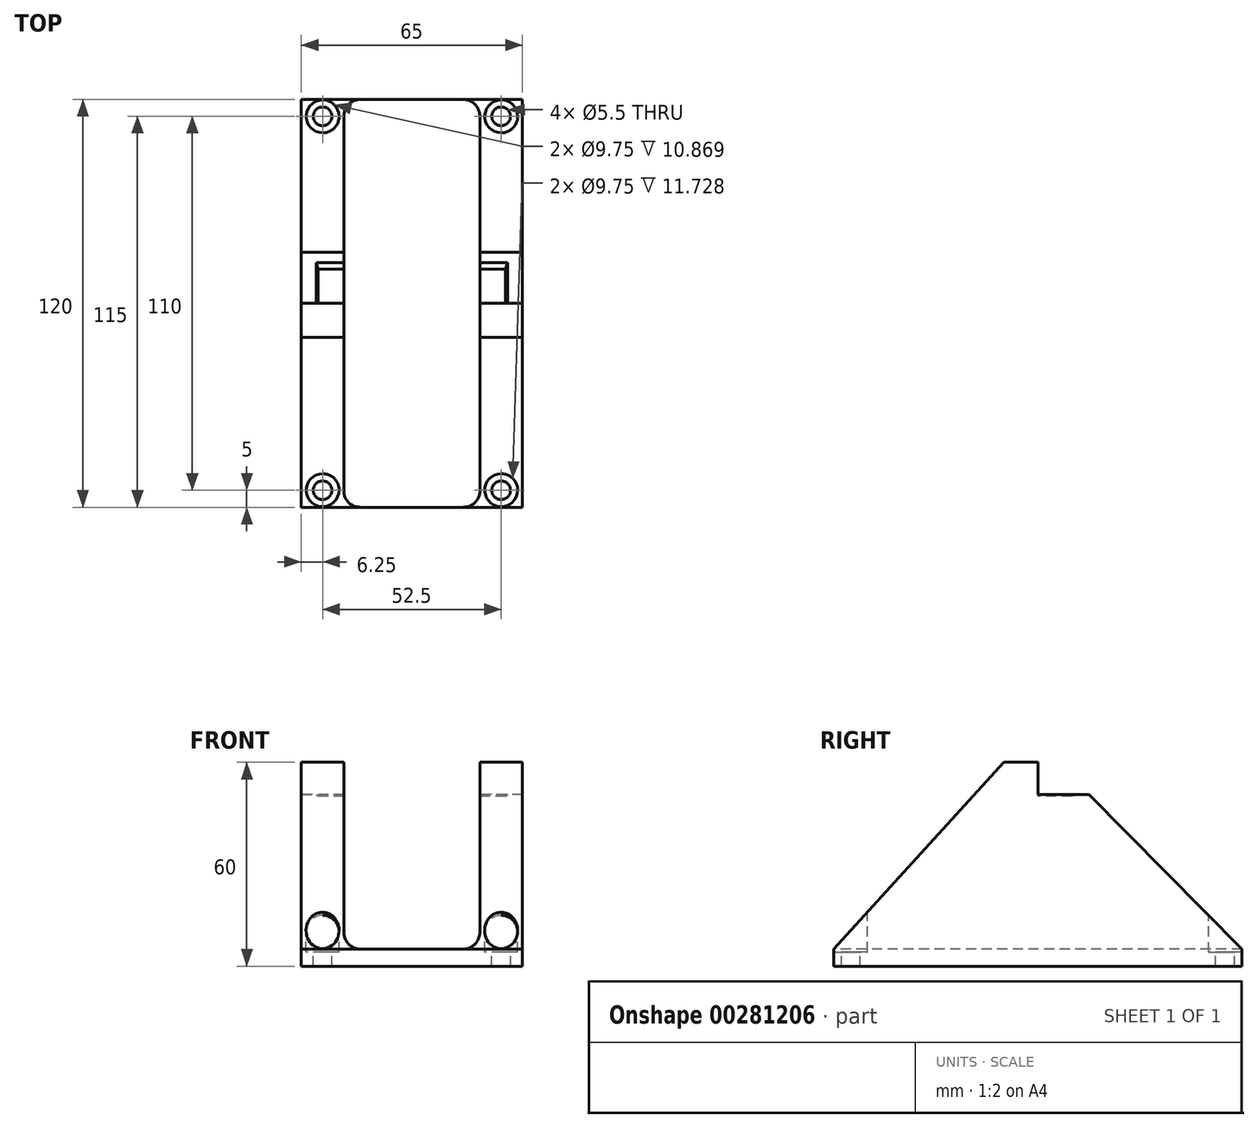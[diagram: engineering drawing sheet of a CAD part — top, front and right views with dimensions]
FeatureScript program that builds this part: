
annotation { "Feature Type Name" : "Feature", "Feature Type Description" : "" }
export const myFeature = defineFeature(function(context is Context, id is Id, definition is map)
    precondition{}
    {
        {
            var Q0;
            Q0=qCreatedBy(makeId("Right.planeOp"),FACE);
            var sketch = newSketch(context, id + "F0", { "sketchPlane" : qUnion([Q0])});
            skLineSegment(sketch, "E0", {"start": v(0, 60) * mm, "end": v(0, 50) * mm});
            skLineSegment(sketch, "E1", {"start": v(0, 50) * mm, "end": v(10, 50) * mm});
            skLineSegment(sketch, "E2", {"start": v(10, 50) * mm, "end": v(12, 50.54) * mm});
            skLineSegment(sketch, "E3", {"start": v(12, 50.54) * mm, "end": v(15, 50.54) * mm});
            skLineSegment(sketch, "E4", {"start": v(60, 0) * mm, "end": v(-60, 0) * mm});
            skLineSegment(sketch, "E5", {"start": v(-10, 60) * mm, "end": v(0, 60) * mm});
            skLineSegment(sketch, "E6", {"start": v(-60, 0) * mm, "end": v(-60, 5) * mm});
            skLineSegment(sketch, "E7", {"start": v(-60, 5) * mm, "end": v(-10, 60) * mm});
            skLineSegment(sketch, "E8", {"start": v(60, 0) * mm, "end": v(60, 5) * mm});
            skLineSegment(sketch, "E9", {"start": v(60, 5) * mm, "end": v(15, 50.54) * mm});
            skPoint(sketch, "E10", {"position": v(0, 0) * mm});
            skSolve(sketch);
        }
        {
            var Q0;
            Q0 = qSketchRegion(id + "F0", true);
            extrude(context, id + "F1", {"entities" : qUnion([Q0]), "endBound" : BoundingType.SYMMETRIC, "depth" : 65 * mm, "offsetDistance" : 25 * mm});
        }
        {
            var Q0;
            Q0=qCreatedBy(makeId("Front.planeOp"),FACE);
            var sketch = newSketch(context, id + "F2", { "sketchPlane" : qUnion([Q0])});
            skLineSegment(sketch, "E11.bottom", {"start": v(20, 5) * mm, "end": v(-20, 5) * mm});
            skLineSegment(sketch, "E11.top", {"start": v(20, 60) * mm, "end": v(-20, 60) * mm});
            skLineSegment(sketch, "E11.left", {"start": v(20, 5) * mm, "end": v(20, 60) * mm});
            skLineSegment(sketch, "E11.right", {"start": v(-20, 5) * mm, "end": v(-20, 60) * mm});
            skPoint(sketch, "E11.middle", {"position": v(0, 32.5) * mm});
            skSolve(sketch);
        }
        {
            var Q0;
            Q0 = qSketchRegion(id + "F2", true);
            extrude(context, id + "F3", {"entities" : qUnion([Q0]), "operationType" : NewBodyOperationType.REMOVE, "endBound" : BoundingType.THROUGH_ALL, "oppositeDirection" : true, "depth" : 25 * mm, "offsetDistance" : 25 * mm, "hasSecondDirection" : true, "secondDirectionBound" : SecondDirectionBoundingType.THROUGH_ALL, "secondDirectionOppositeDirection" : false, "secondDirectionDepth" : 25 * mm});
        }
        {
            var Q0;
            Q0=makeQuery(id+"F3.boolean.opBoolean","COPY",EDGE,{"derivedFrom":makeQuery(id+"F3.opExtrude","SWEPT_EDGE",EDGE,{"disambiguationData":[OSD([sQuery(id+"F2.wireOp",EDGE,"E11.bottom"),sQuery(id+"F2.wireOp",EDGE,"E11.left")])]})});
            var Q1;
            Q1=makeQuery(id+"F3.boolean.opBoolean","COPY",EDGE,{"derivedFrom":makeQuery(id+"F3.opExtrude","SWEPT_EDGE",EDGE,{"disambiguationData":[OSD([sQuery(id+"F2.wireOp",EDGE,"E11.bottom"),sQuery(id+"F2.wireOp",EDGE,"E11.right")])]})});
            fillet(context, id + "F4", {"entities" : qUnion([Q0, Q1]), "radius" : 5 * mm, "tangentPropagation" : true, "allowEdgeOverflow" : false});
        }
        {
            var Q0;
            {var subQ2=sQuery(id+"F0.wireOp",EDGE,"E1");Q0=makeQuery(id+"F3.boolean.opBoolean","SPLIT",FACE,{"disambiguationData":[TD([makeQuery(id+"F3.opExtrude","SWEPT_FACE",FACE,{"disambiguationData":[OSD([sQuery(id+"F2.wireOp",EDGE,"E11.right")])]})])],"derivedFrom":makeQuery(id+"F1.opExtrude","SWEPT_FACE",FACE,{"disambiguationData":[OSD([subQ2])]})});}
            var sketch = newSketch(context, id + "F5", { "sketchPlane" : qUnion([Q0])});
            skLineSegment(sketch, "E12.bottom", {"start": v(-26.25, 55) * mm, "end": v(26.25, 55) * mm, "construction": true});
            skLineSegment(sketch, "E12.top", {"start": v(-26.25, -55) * mm, "end": v(26.25, -55) * mm, "construction": true});
            skLineSegment(sketch, "E12.left", {"start": v(-26.25, 55) * mm, "end": v(-26.25, -55) * mm, "construction": true});
            skLineSegment(sketch, "E12.right", {"start": v(26.25, 55) * mm, "end": v(26.25, -55) * mm, "construction": true});
            skPoint(sketch, "E12.middle", {"position": v(0, 0) * mm});
            skPoint(sketch, "E13", {"position": v(-26.25, 55) * mm});
            skPoint(sketch, "E14", {"position": v(26.25, 55) * mm});
            skPoint(sketch, "E15", {"position": v(26.25, -55) * mm});
            skPoint(sketch, "E16", {"position": v(-26.25, -55) * mm});
            skSolve(sketch);
        }
        {
            var Q0;
            Q0=sQuery(id+"F5.wireOp",VERTEX,"E13");
            var Q1;
            Q1=sQuery(id+"F5.wireOp",VERTEX,"E14");
            var Q2;
            Q2=sQuery(id+"F5.wireOp",VERTEX,"E16");
            var Q3;
            Q3=sQuery(id+"F5.wireOp",VERTEX,"E15");
            var Q4;
            Q4=makeQuery(id+"F1.opExtrude","SWEPT_BODY",BODY,{"disambiguationData":[OSD([sQuery(id+"F0.wireOp",EDGE,"E0"),sQuery(id+"F0.wireOp",EDGE,"E1"),sQuery(id+"F0.wireOp",EDGE,"E2"),sQuery(id+"F0.wireOp",EDGE,"E3"),sQuery(id+"F0.wireOp",EDGE,"E4"),sQuery(id+"F0.wireOp",EDGE,"E5"),sQuery(id+"F0.wireOp",EDGE,"E6"),sQuery(id+"F0.wireOp",EDGE,"E7"),sQuery(id+"F0.wireOp",EDGE,"E8"),sQuery(id+"F0.wireOp",EDGE,"E9")])]});
            hole(context, id + "F6", {"style" : HoleStyle.C_BORE, "endStyle" : HoleEndStyle.THROUGH, "holeDiameter" : 5.5 * mm, "cBoreDiameter" : 9.75 * mm, "cBoreDepth" : 1 * mm, "majorDiameter" : 5 * mm, "isTappedThrough" : true, "tappedDepth" : 12 * mm, "tapClearance" : 3, "locations" : qUnion([Q0, Q1, Q2, Q3]), "scope" : qUnion([Q4])});
        }
        {
            var Q0;
            {var subQ2=sQuery(id+"F0.wireOp",EDGE,"E1");Q0=makeQuery(id+"F3.boolean.opBoolean","SPLIT",FACE,{"disambiguationData":[TD([makeQuery(id+"F3.opExtrude","SWEPT_FACE",FACE,{"disambiguationData":[OSD([sQuery(id+"F2.wireOp",EDGE,"E11.left")])]})])],"derivedFrom":makeQuery(id+"F1.opExtrude","SWEPT_FACE",FACE,{"disambiguationData":[OSD([subQ2])]})});}
            var sketch = newSketch(context, id + "F7", { "sketchPlane" : qUnion([Q0])});
            skLineSegment(sketch, "E17.bottom", {"start": v(-32.5, 0) * mm, "end": v(-27.5, 0) * mm});
            skLineSegment(sketch, "E17.top", {"start": v(-32.5, 12) * mm, "end": v(-27.5, 12) * mm});
            skLineSegment(sketch, "E17.left", {"start": v(-32.5, 0) * mm, "end": v(-32.5, 12) * mm});
            skLineSegment(sketch, "E17.right", {"start": v(-27.5, 0) * mm, "end": v(-27.5, 12) * mm});
            skLineSegment(sketch, "E18", {"start": v(0, 0) * mm, "end": v(0, 44.26) * mm, "construction": true});
            skLineSegment(sketch, "E19.MirrorCS", {"start": v(32.5, 0) * mm, "end": v(27.5, 0) * mm});
            skLineSegment(sketch, "E20.MirrorCS", {"start": v(32.5, 12) * mm, "end": v(27.5, 12) * mm});
            skLineSegment(sketch, "E21.MirrorCS", {"start": v(32.5, 0) * mm, "end": v(32.5, 12) * mm});
            skLineSegment(sketch, "E22.MirrorCS", {"start": v(27.5, 0) * mm, "end": v(27.5, 12) * mm});
            skSolve(sketch);
        }
        {
            var Q0;
            Q0 = qSketchRegion(id + "F7", true);
            var Q1;
            {var subQ1=sQuery(id+"F0.wireOp",EDGE,"E3");Q1=makeQuery(id+"F3.boolean.opBoolean","SPLIT",FACE,{"disambiguationData":[TD([makeQuery(id+"F3.opExtrude","SWEPT_FACE",FACE,{"disambiguationData":[OSD([sQuery(id+"F2.wireOp",EDGE,"E11.left")])]})])],"derivedFrom":makeQuery(id+"F1.opExtrude","SWEPT_FACE",FACE,{"disambiguationData":[OSD([subQ1])]})});}
            extrude(context, id + "F8", {"entities" : qUnion([Q0]), "operationType" : NewBodyOperationType.ADD, "endBound" : BoundingType.UP_TO_SURFACE, "depth" : 25 * mm, "endBoundEntityFace" : qUnion([Q1]), "offsetDistance" : 25 * mm});
        }
        {
            var Q0;
            Q0=makeQuery(id+"F8.opExtrude","CAP_EDGE",EDGE,{"disambiguationData":[OSD([sQuery(id+"F7.wireOp",EDGE,"E22.MirrorCS")])],"isStart":false});
            var Q1;
            Q1=makeQuery(id+"F8.opExtrude","CAP_EDGE",EDGE,{"disambiguationData":[OSD([sQuery(id+"F7.wireOp",EDGE,"E17.right")])],"isStart":false});
            chamfer(context, id + "F9", {"entities" : qUnion([Q0, Q1]), "chamferType" : ChamferType.OFFSET_ANGLE, "width" : 0.6 * mm, "oppositeDirection" : true, "angle" : 45 * degree, "tangentPropagation" : true});
        }
        {
            var Q0;
            {var subQ2=sQuery(id+"F0.wireOp",EDGE,"E0");Q0=makeQuery(id+"F3.boolean.opBoolean","SPLIT",FACE,{"disambiguationData":[TD([makeQuery(id+"F3.opExtrude","SWEPT_FACE",FACE,{"disambiguationData":[OSD([sQuery(id+"F2.wireOp",EDGE,"E11.left")])]})])],"derivedFrom":makeQuery(id+"F1.opExtrude","SWEPT_FACE",FACE,{"disambiguationData":[OSD([subQ2])]})});}
            var sketch = newSketch(context, id + "F10", { "sketchPlane" : qUnion([Q0])});
            skLineSegment(sketch, "E23", {"start": v(-20, 60) * mm, "end": v(20, 50) * mm, "construction": true});
            skPoint(sketch, "E24", {"position": v(0, 55) * mm});
            skSolve(sketch);
        }
    });
